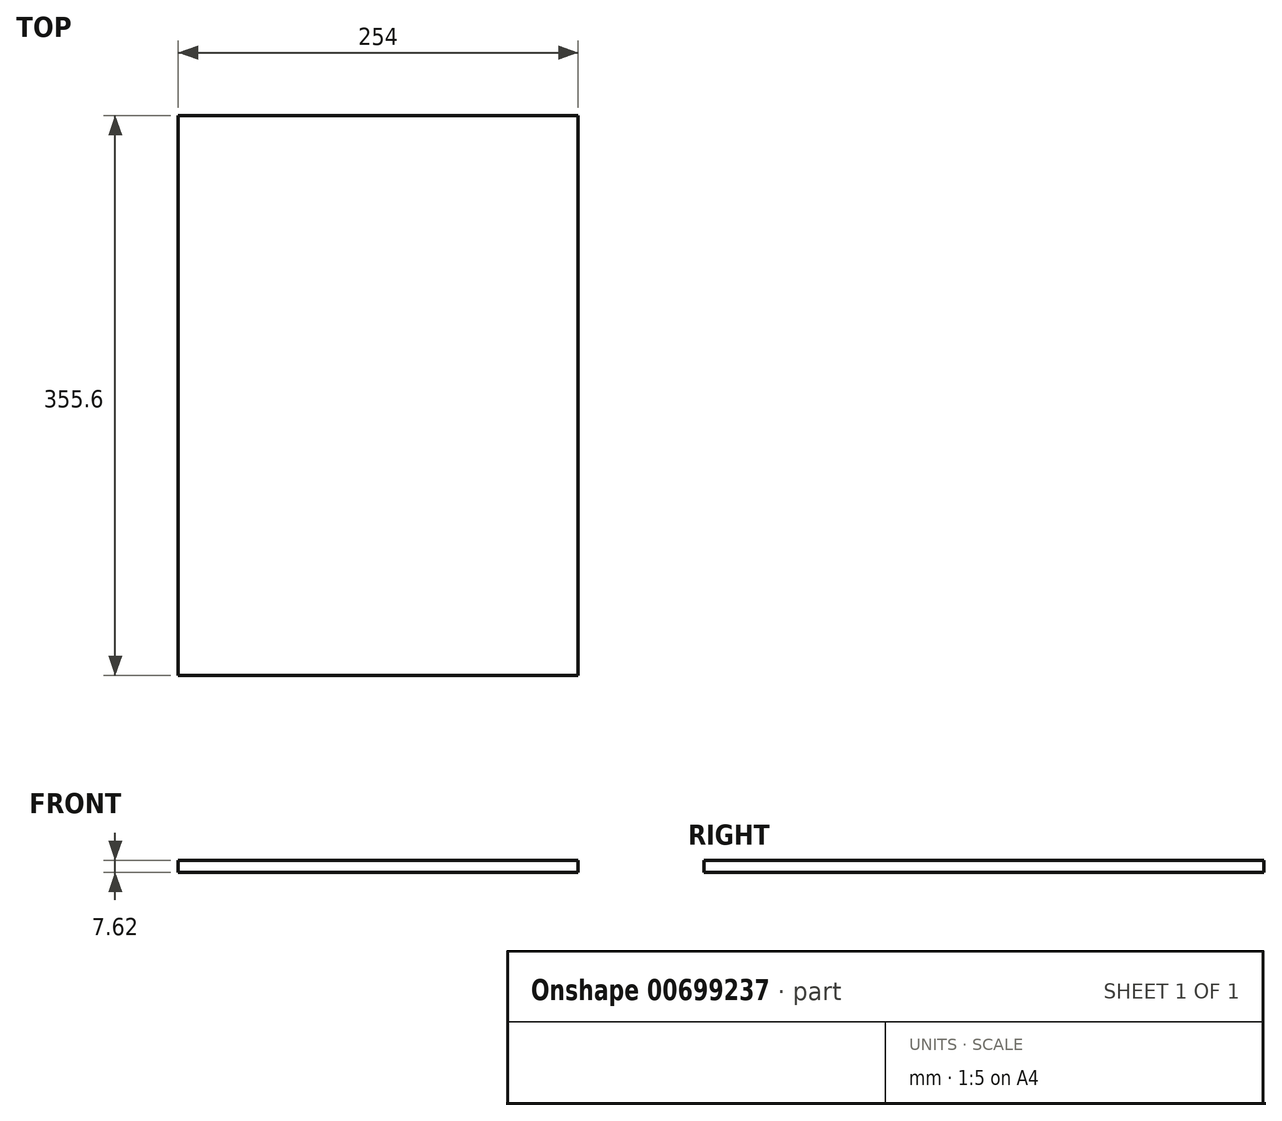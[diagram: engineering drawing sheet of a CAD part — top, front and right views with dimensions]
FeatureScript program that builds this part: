
annotation { "Feature Type Name" : "Feature", "Feature Type Description" : "" }
export const myFeature = defineFeature(function(context is Context, id is Id, definition is map)
    precondition{}
    {
        {
            var Q0;
            Q0=qCreatedBy(makeId("Front.planeOp"),FACE);
            var sketch = newSketch(context, id + "F0", { "sketchPlane" : qUnion([Q0])});
            skLineSegment(sketch, "E0", {"start": v(-254, -38.47) * mm, "end": v(0, -38.47) * mm});
            skLineSegment(sketch, "E1", {"start": v(0, -38.47) * mm, "end": v(0, -30.85) * mm});
            skLineSegment(sketch, "E2", {"start": v(0, -30.85) * mm, "end": v(-254, -30.85) * mm});
            skLineSegment(sketch, "E3", {"start": v(-254, -30.85) * mm, "end": v(-254, -38.47) * mm});
            skSolve(sketch);
        }
        {
            var Q0;
            Q0=makeQuery(id+"F0.imprint","IMPRINT",FACE,{"disambiguationData":[TD([[makeQuery(id+"F0.imprint","IMPRINT",EDGE,{"derivedFrom":sQuery(id+"F0.wireOp",EDGE,"E0")}),1.0]])]});
            extrude(context, id + "F1", {"entities" : qUnion([Q0]), "depth" : 355.6 * mm, "offsetDistance" : 25.4 * mm});
        }
    });
